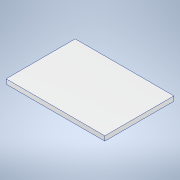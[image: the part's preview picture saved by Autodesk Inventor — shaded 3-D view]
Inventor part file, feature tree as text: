
AUTODESK INVENTOR PART (.ipt)
format: ipt  version: 2022 (Build 260153000, 153)  size: 92,672 bytes
history: native  units: mm
features: extrude x1, sketch x1
ambient origin geometry x8: Origin, YZ Plane, XZ Plane, XY Plane, X Axis, Y Axis, Z Axis, Center Point
bodies: Solid1 (feature_tree)
feature tree (2):
  extrude  "Extrusion1"  Depth=300.0mm
  sketch  "Sketch1"  dims[d0=210.0mm d1=300.0mm d2=14.0mm d3=0.0mm]
